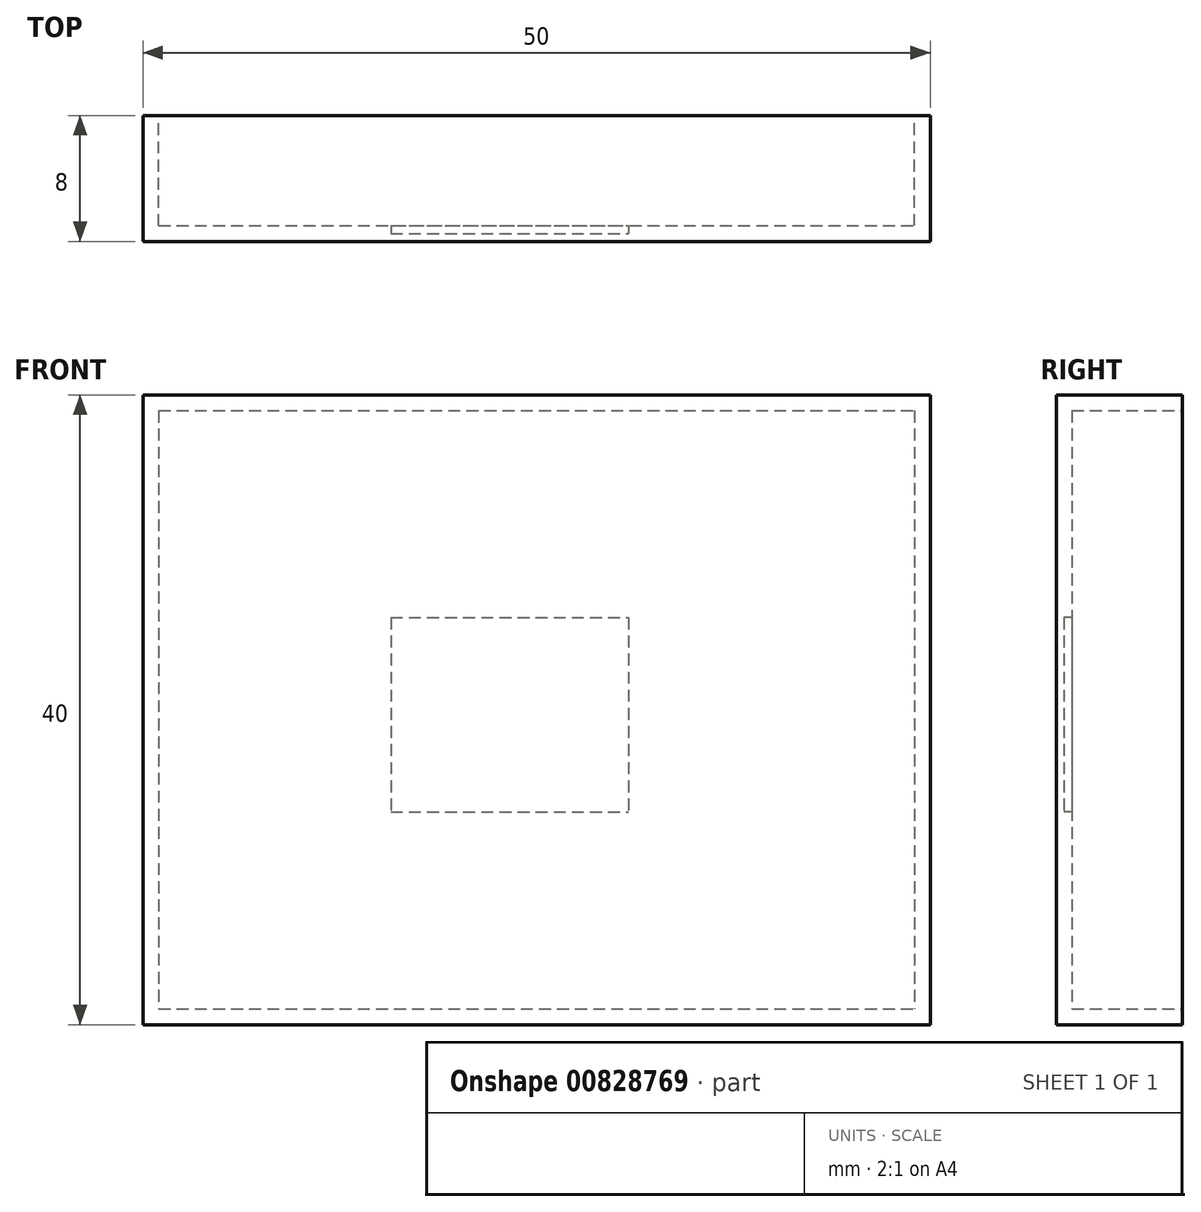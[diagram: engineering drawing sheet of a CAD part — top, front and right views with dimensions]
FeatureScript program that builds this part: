
annotation { "Feature Type Name" : "Feature", "Feature Type Description" : "" }
export const myFeature = defineFeature(function(context is Context, id is Id, definition is map)
    precondition{}
    {
        {
            var Q0;
            Q0=qCreatedBy(makeId("Front.planeOp"),FACE);
            var sketch = newSketch(context, id + "F0", { "sketchPlane" : qUnion([Q0])});
            skLineSegment(sketch, "E0.bottom", {"start": v(-30.82, 20.15) * mm, "end": v(19.18, 20.15) * mm});
            skLineSegment(sketch, "E0.top", {"start": v(-30.82, -19.85) * mm, "end": v(19.18, -19.85) * mm});
            skLineSegment(sketch, "E0.left", {"start": v(-30.82, 20.15) * mm, "end": v(-30.82, -19.85) * mm});
            skLineSegment(sketch, "E0.right", {"start": v(19.18, 20.15) * mm, "end": v(19.18, -19.85) * mm});
            skSolve(sketch);
        }
        {
            var Q0;
            Q0=makeQuery(id+"F0.imprint","IMPRINT",FACE,{"disambiguationData":[TD([[makeQuery(id+"F0.imprint","IMPRINT",EDGE,{"derivedFrom":sQuery(id+"F0.wireOp",EDGE,"E0.bottom")}),-1.0]])]});
            extrude(context, id + "F1", {"entities" : qUnion([Q0]), "depth" : 8 * mm, "offsetDistance" : 25 * mm});
        }
        {
            var Q0;
            Q0=makeQuery(id+"F1.opExtrude","CAP_FACE",FACE,{"disambiguationData":[OSD([sQuery(id+"F0.wireOp",EDGE,"E0.bottom"),sQuery(id+"F0.wireOp",EDGE,"E0.top"),sQuery(id+"F0.wireOp",EDGE,"E0.left"),sQuery(id+"F0.wireOp",EDGE,"E0.right")])],"isStart":true});
            shell(context, id + "F2", {"entities" : qUnion([Q0]), "thickness" : 1 * mm});
        }
        {
            var Q0;
            Q0=makeQuery(id+"F2.opShell","OFFSET_FACE",FACE,{"disambiguationData":[OSD([sQuery(id+"F0.wireOp",EDGE,"E0.bottom"),sQuery(id+"F0.wireOp",EDGE,"E0.top"),sQuery(id+"F0.wireOp",EDGE,"E0.left"),sQuery(id+"F0.wireOp",EDGE,"E0.right")])]});
            var sketch = newSketch(context, id + "F3", { "sketchPlane" : qUnion([Q0])});
            skLineSegment(sketch, "E1.bottom", {"start": v(15.08, 6.02) * mm, "end": v(0, 6.02) * mm});
            skLineSegment(sketch, "E1.top", {"start": v(15.08, -6.32) * mm, "end": v(0, -6.32) * mm});
            skLineSegment(sketch, "E1.left", {"start": v(15.08, 6.02) * mm, "end": v(15.08, -6.32) * mm});
            skLineSegment(sketch, "E1.right", {"start": v(0, 6.02) * mm, "end": v(0, -6.32) * mm});
            skSolve(sketch);
        }
        {
            var Q0;
            Q0=makeQuery(id+"F3.imprint","IMPRINT",FACE,{"disambiguationData":[TD([[makeQuery(id+"F3.imprint","IMPRINT",EDGE,{"derivedFrom":sQuery(id+"F3.wireOp",EDGE,"E1.bottom")}),1.0]])]});
            extrude(context, id + "F4", {"entities" : qUnion([Q0]), "operationType" : NewBodyOperationType.ADD, "depth" : 10 * mm, "offsetDistance" : 25 * mm});
        }
        {
            var Q0;
            Q0=makeQuery(id+"F4.opExtrude","CAP_FACE",FACE,{"disambiguationData":[OSD([sQuery(id+"F3.wireOp",EDGE,"E1.bottom"),sQuery(id+"F3.wireOp",EDGE,"E1.top"),sQuery(id+"F3.wireOp",EDGE,"E1.left"),sQuery(id+"F3.wireOp",EDGE,"E1.right")])],"isStart":false});
            var Q1;
            Q1=makeQuery(id+"F4.opExtrude","SWEPT_FACE",FACE,{"disambiguationData":[OSD([sQuery(id+"F3.wireOp",EDGE,"E1.right")])]});
            var Q2;
            Q2=makeQuery(id+"F4.opExtrude","SWEPT_FACE",FACE,{"disambiguationData":[OSD([sQuery(id+"F3.wireOp",EDGE,"E1.top")])]});
            var Q3;
            Q3=makeQuery(id+"F4.opExtrude","SWEPT_FACE",FACE,{"disambiguationData":[OSD([sQuery(id+"F3.wireOp",EDGE,"E1.bottom")])]});
            var Q4;
            Q4=makeQuery(id+"F4.opExtrude","SWEPT_FACE",FACE,{"disambiguationData":[OSD([sQuery(id+"F3.wireOp",EDGE,"E1.left")])]});
            shell(context, id + "F5", {"entities" : qUnion([Q0, Q1, Q2, Q3, Q4]), "thickness" : 0.5 * mm});
        }
    });
